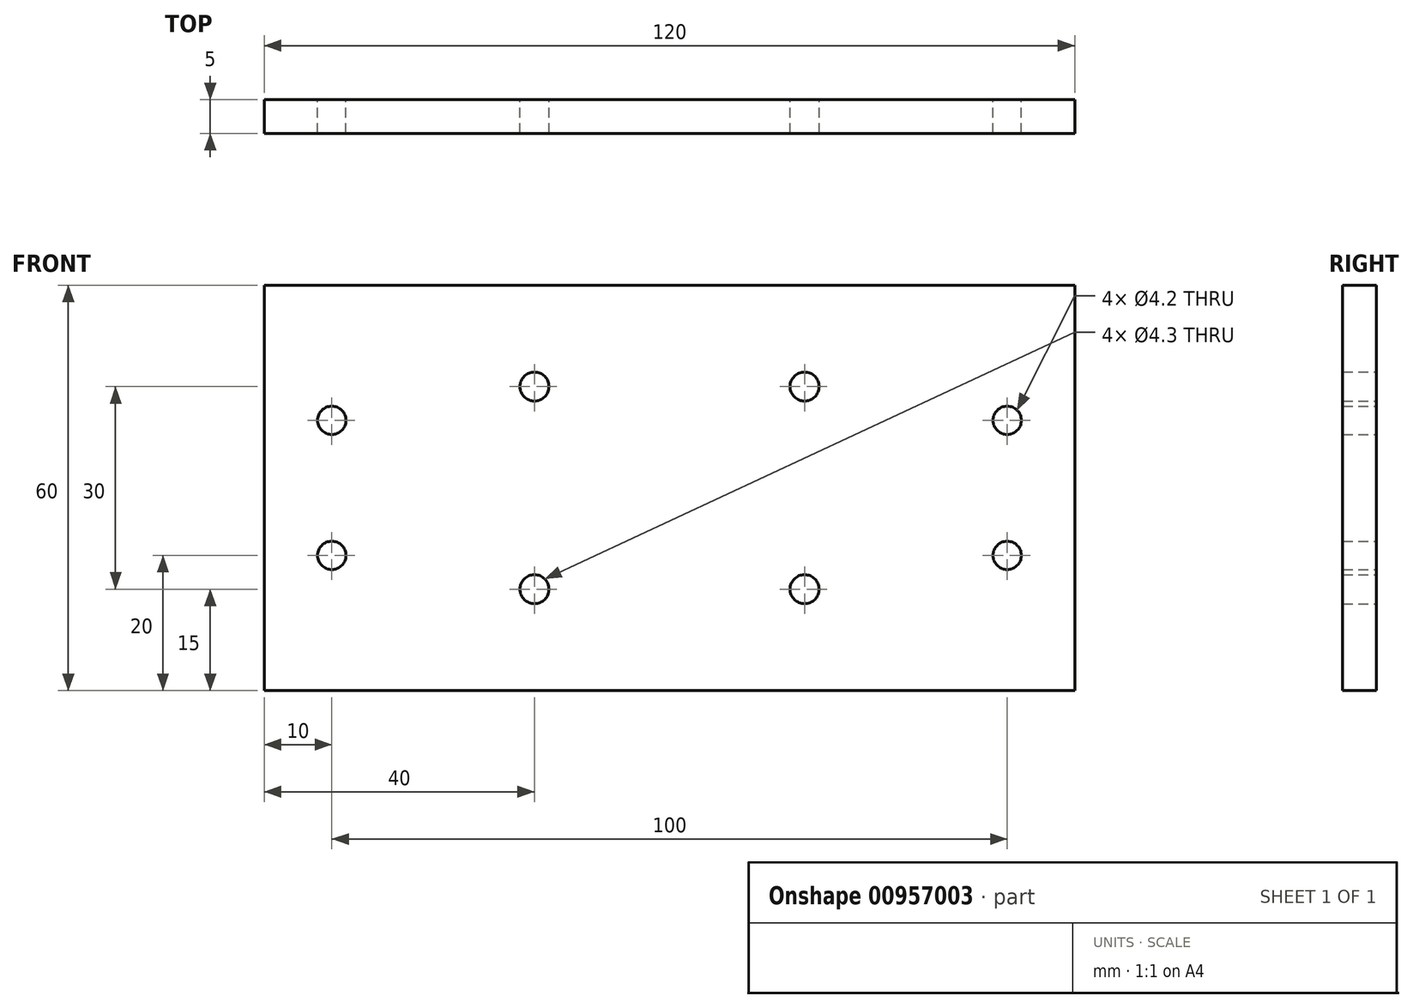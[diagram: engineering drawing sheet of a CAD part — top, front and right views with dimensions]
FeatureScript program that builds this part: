
annotation { "Feature Type Name" : "Feature", "Feature Type Description" : "" }
export const myFeature = defineFeature(function(context is Context, id is Id, definition is map)
    precondition{}
    {
        {
            var Q0;
            Q0=qCreatedBy(makeId("Front.planeOp"),FACE);
            var sketch = newSketch(context, id + "F0", { "sketchPlane" : qUnion([Q0])});
            skLineSegment(sketch, "E0.bottom", {"start": v(0, 0) * mm, "end": v(120, 0) * mm});
            skLineSegment(sketch, "E0.top", {"start": v(0, 60) * mm, "end": v(120, 60) * mm});
            skLineSegment(sketch, "E0.left", {"start": v(0, 0) * mm, "end": v(0, 60) * mm});
            skLineSegment(sketch, "E0.right", {"start": v(120, 0) * mm, "end": v(120, 60) * mm});
            skSolve(sketch);
        }
        {
            var Q0;
            Q0 = qSketchRegion(id + "F0", true);
            extrude(context, id + "F1", {"entities" : qUnion([Q0]), "depth" : 5 * mm, "offsetDistance" : 25 * mm});
        }
        {
            var Q0;
            Q0=qCreatedBy(makeId("Front.planeOp"),FACE);
            var sketch = newSketch(context, id + "F2", { "sketchPlane" : qUnion([Q0])});
            skPoint(sketch, "E1", {"position": v(10, 20) * mm});
            skPoint(sketch, "E2", {"position": v(10, 40) * mm});
            skPoint(sketch, "E3", {"position": v(110, 20) * mm});
            skPoint(sketch, "E4", {"position": v(110, 40) * mm});
            skSolve(sketch);
        }
        {
            var Q0;
            Q0=sQuery(id+"F2.wireOp",VERTEX,"E2");
            var Q1;
            Q1=sQuery(id+"F2.wireOp",VERTEX,"E1");
            var Q2;
            Q2=sQuery(id+"F2.wireOp",VERTEX,"E3");
            var Q3;
            Q3=sQuery(id+"F2.wireOp",VERTEX,"E4");
            var Q4;
            Q4=makeQuery(id+"F1.opExtrude","SWEPT_BODY",BODY,{"disambiguationData":[OSD([sQuery(id+"F0.wireOp",EDGE,"E0.bottom"),sQuery(id+"F0.wireOp",EDGE,"E0.top"),sQuery(id+"F0.wireOp",EDGE,"E0.left"),sQuery(id+"F0.wireOp",EDGE,"E0.right")])]});
            hole(context, id + "F3", {"style" : HoleStyle.SIMPLE, "endStyle" : HoleEndStyle.THROUGH, "oppositeDirection" : true, "standardTappedOrClearance" : lookupTablePath({ "standard" : "ISO", "engagement" : "75%", "pitch" : "0.8 mm", "size" : "M5", "type" : "Tapped" }), "standardBlindInLast" : lookupTablePath({ "standard" : "ISO", "fit" : "Normal", "engagement" : "75%", "pitch" : "0.8 mm", "size" : "M5", "type" : "Clearance & tapped" }), "holeDiameter" : 4.2 * mm, "majorDiameter" : 5 * mm, "showTappedDepth" : true, "isTappedThrough" : true, "tappedDepth" : 12 * mm, "tapClearance" : 3, "locations" : qUnion([Q0, Q1, Q2, Q3]), "scope" : qUnion([Q4])});
        }
        {
            var Q0;
            Q0=qCreatedBy(makeId("Front.planeOp"),FACE);
            var sketch = newSketch(context, id + "F4", { "sketchPlane" : qUnion([Q0])});
            skPoint(sketch, "E5", {"position": v(40, 15) * mm});
            skPoint(sketch, "E6", {"position": v(40, 45) * mm});
            skPoint(sketch, "E7", {"position": v(80, 15) * mm});
            skPoint(sketch, "E8", {"position": v(80, 45) * mm});
            skLineSegment(sketch, "E9", {"start": v(40, 45) * mm, "end": v(80, 45) * mm});
            skPoint(sketch, "E10", {"position": v(60, 45) * mm});
            skLineSegment(sketch, "E11", {"start": v(80, 45) * mm, "end": v(80, 15) * mm});
            skPoint(sketch, "E12", {"position": v(80, 30) * mm});
            skSolve(sketch);
        }
        {
            var Q0;
            Q0=sQuery(id+"F4.wireOp",VERTEX,"E6");
            var Q1;
            Q1=sQuery(id+"F4.wireOp",VERTEX,"E5");
            var Q2;
            Q2=sQuery(id+"F4.wireOp",VERTEX,"E7");
            var Q3;
            Q3=sQuery(id+"F4.wireOp",VERTEX,"E8");
            var Q4;
            Q4=makeQuery(id+"F1.opExtrude","SWEPT_BODY",BODY,{"disambiguationData":[OSD([sQuery(id+"F0.wireOp",EDGE,"E0.bottom"),sQuery(id+"F0.wireOp",EDGE,"E0.top"),sQuery(id+"F0.wireOp",EDGE,"E0.left"),sQuery(id+"F0.wireOp",EDGE,"E0.right")])]});
            hole(context, id + "F5", {"style" : HoleStyle.SIMPLE, "endStyle" : HoleEndStyle.THROUGH, "oppositeDirection" : true, "standardTappedOrClearance" : lookupTablePath({ "standard" : "ISO", "size" : "4.3", "type" : "Drilled" }), "standardBlindInLast" : lookupTablePath({ "standard" : "ISO", "size" : "4.3", "type" : "Drilled" }), "holeDiameter" : 4.3 * mm, "majorDiameter" : 5 * mm, "isTappedThrough" : true, "tappedDepth" : 12 * mm, "tapClearance" : 3, "locations" : qUnion([Q0, Q1, Q2, Q3]), "scope" : qUnion([Q4])});
        }
    });
